# Revit family: GQ Rosenberg 3
name_source: partatom
category: Wyposażenie mechaniczne
revit_build: Autodesk Revit 2017 (Build: 20160225_1515(x64)
units: mm (PartAtom-declared; Revit-internal decimal feet)

## family parameters
Oparty na płaszczyźnie roboczej = Nie
Punkt obliczania pomieszczeń = Nie
Tnij formami wycięć po wczytaniu = Nie
Typ części = Normalny
Współdzielony = Nie
Wymiar okrągłego złącza = Użyj średnicy
Zawsze pionowo = Tak

## types (6) — shared parameters
Częstotliwość = 50 Hz
Grubosc_plyty = 20 mm  [stored 0.0656168 ft]
Klasa szczelnosci silnika (IP) = IP54
Producent = Rosenberg

## per-type parameters (varying)
- 630 K.6FF KK: 1000 K.6NA KK=Nie; 630 N.5HF KK=Tak; 710 K.6IF KK=Nie; 800 K.6IF KK=Tak; Ciśnienie=331.0 Pa; Dlugosc_silnika_przod=80 mm  [stored 0.262467 ft]; Dlugosc_silnika_tyl=50 mm  [stored 0.164042 ft]; Dlugosc_smigla=309 mm  [stored 1.01378 ft]; Grubosc=130 mm  [stored 0.426509 ft]; Maksymalna dopuszczalna temperatura przetłaczanego medium=45 °C; Masa=34.00 kg; Moc=3 kW; Model=630 K.6FF KK; Napięcie=400 V; Obroty (1/min)=1530; Promien_wew=314 mm  [stored 1.03018 ft]; Promien_zew=342 mm; Przepływ poowietrza=11276.0 m³/h; Prąd=4 A; S1=35 mm  [stored 0.114829 ft]; Srednica_silnika=50 mm  [stored 0.164042 ft]; Srednica_wew=627 mm  [stored 2.05709 ft]; Srednica_zewnetrzna=683 mm  [stored 2.24081 ft]; Wymiar_obudowy=805 mm  [stored 2.64108 ft]; Wymiar_obudowy/2=403 mm
- 1000 K.6NA KK: 1000 K.6NA KK=Tak; 630 N.5HF KK=Nie; 710 K.6IF KK=Nie; 800 K.6IF KK=Nie; Ciśnienie=121.0 Pa; Dlugosc_silnika_przod=80 mm  [stored 0.262467 ft]; Dlugosc_silnika_tyl=50 mm  [stored 0.164042 ft]; Dlugosc_smigla=490 mm  [stored 1.60761 ft]; Grubosc=197 mm; Maksymalna dopuszczalna temperatura przetłaczanego medium=60 °C; Masa=65.00 kg; Moc=2 kW; Model=560 K.5HF KS; Napięcie=400 V; Obroty (1/min)=670; Promien_wew=495 mm  [stored 1.62402 ft]; Promien_zew=532 mm  [stored 1.74541 ft]; Przepływ poowietrza=22086.0 m³/h; Prąd=3 A; S1=0 mm  [stored 0 ft]; Srednica_silnika=90 mm  [stored 0.295276 ft]; Srednica_wew=990 mm; Srednica_zewnetrzna=1064 mm; Wymiar_obudowy=1170 mm; Wymiar_obudowy/2=585 mm  [stored 1.91929 ft]
- 630 N.5HF KS: 1000 K.6NA KK=Nie; 630 N.5HF KK=Tak; 710 K.6IF KK=Nie; 800 K.6IF KK=Tak; Ciśnienie=150.0 Pa; Dlugosc_silnika_przod=50 mm  [stored 0.164042 ft]; Dlugosc_silnika_tyl=50 mm  [stored 0.164042 ft]; Dlugosc_smigla=309 mm  [stored 1.01378 ft]; Grubosc=126 mm  [stored 0.413386 ft]; Maksymalna dopuszczalna temperatura przetłaczanego medium=60 °C; Masa=25.00 kg; Moc=1 kW; Model=630 K.6FF KK; Napięcie=230 V; Obroty (1/min)=1080; Promien_wew=314 mm  [stored 1.03018 ft]; Promien_zew=342 mm; Przepływ poowietrza=9312.0 m³/h; Prąd=4 A; S1=10 mm  [stored 0.0328084 ft]; Srednica_silnika=68 mm; Srednica_wew=628 mm  [stored 2.06037 ft]; Srednica_zewnetrzna=683 mm  [stored 2.24081 ft]; URL=https://www.rosenberg.pl; Wymiar_obudowy=805 mm  [stored 2.64108 ft]; Wymiar_obudowy/2=403 mm
- 630 N.5HF KK: 1000 K.6NA KK=Nie; 630 N.5HF KK=Tak; 710 K.6IF KK=Nie; 800 K.6IF KK=Tak; Ciśnienie=141.0 Pa; Dlugosc_silnika_przod=50 mm  [stored 0.164042 ft]; Dlugosc_silnika_tyl=50 mm  [stored 0.164042 ft]; Dlugosc_smigla=309 mm  [stored 1.01378 ft]; Grubosc=126 mm  [stored 0.413386 ft]; Maksymalna dopuszczalna temperatura przetłaczanego medium=60 °C; Masa=24.50 kg; Moc=1 kW; Model=630 N.5HF KK; Napięcie=400 V; Obroty (1/min)=1050; Promien_wew=314 mm  [stored 1.03018 ft]; Promien_zew=342 mm; Przepływ poowietrza=9003.0 m³/h; Prąd=2 A; S1=10 mm  [stored 0.0328084 ft]; Srednica_silnika=68 mm; Srednica_wew=628 mm  [stored 2.06037 ft]; Srednica_zewnetrzna=683 mm  [stored 2.24081 ft]; URL=https://www.rosenberg.pl; Wymiar_obudowy=805 mm  [stored 2.64108 ft]; Wymiar_obudowy/2=403 mm
- 710 K.6IF KK: 1000 K.6NA KK=Nie; 630 N.5HF KK=Nie; 710 K.6IF KK=Tak; 800 K.6IF KK=Nie; Ciśnienie=244.0 Pa; Dlugosc_silnika_przod=80 mm  [stored 0.262467 ft]; Dlugosc_silnika_tyl=70 mm  [stored 0.229659 ft]; Dlugosc_smigla=347 mm; Grubosc=150 mm; Maksymalna dopuszczalna temperatura przetłaczanego medium=60 °C; Masa=40.50 kg; Moc=3 kW; Model=710 K.6IF KK; Napięcie=400 V; Obroty (1/min)=1250; Promien_wew=352 mm; Promien_zew=386 mm  [stored 1.2664 ft]; Przepływ poowietrza=15508.0 m³/h; Prąd=4 A; S1=35 mm  [stored 0.114829 ft]; Srednica_silnika=50 mm  [stored 0.164042 ft]; Srednica_wew=703 mm  [stored 2.30643 ft]; Srednica_zewnetrzna=772 mm  [stored 2.53281 ft]; URL=https://www.rosenberg.pl; Wymiar_obudowy=850 mm  [stored 2.78871 ft]; Wymiar_obudowy/2=425 mm  [stored 1.39436 ft]
- 800 K.6IF KK: 1000 K.6NA KK=Nie; 630 N.5HF KK=Nie; 710 K.6IF KK=Nie; 800 K.6IF KK=Tak; Ciśnienie=164.0 Pa; Data=08.2018; Dlugosc_silnika_przod=50 mm  [stored 0.164042 ft]; Dlugosc_silnika_tyl=50 mm  [stored 0.164042 ft]; Dlugosc_smigla=389 mm  [stored 1.27625 ft]; Grubosc=190 mm  [stored 0.62336 ft]; Maksymalna dopuszczalna temperatura przetłaczanego medium=60 °C; Masa=48.00 kg; Moc=2 kW; Model=800 K.6IF KK; Napięcie=400 V; Obroty (1/min)=1000; Promien_wew=394 mm; Promien_zew=428 mm  [stored 1.4042 ft]; Przepływ poowietrza=17946.0 m³/h; Prąd=3 A; S1=10 mm  [stored 0.0328084 ft]; Srednica_silnika=65 mm  [stored 0.213255 ft]; Srednica_wew=788 mm; Srednica_zewnetrzna=856 mm  [stored 2.8084 ft]; URL=https://www.rosenberg.pl; Wersja=1; Wymiar_obudowy=970 mm; Wymiar_obudowy/2=485 mm  [stored 1.59121 ft]

note: [stored X ft] marks values corroborated as IEEE doubles in the binary element streams (Revit-internal decimal feet)
